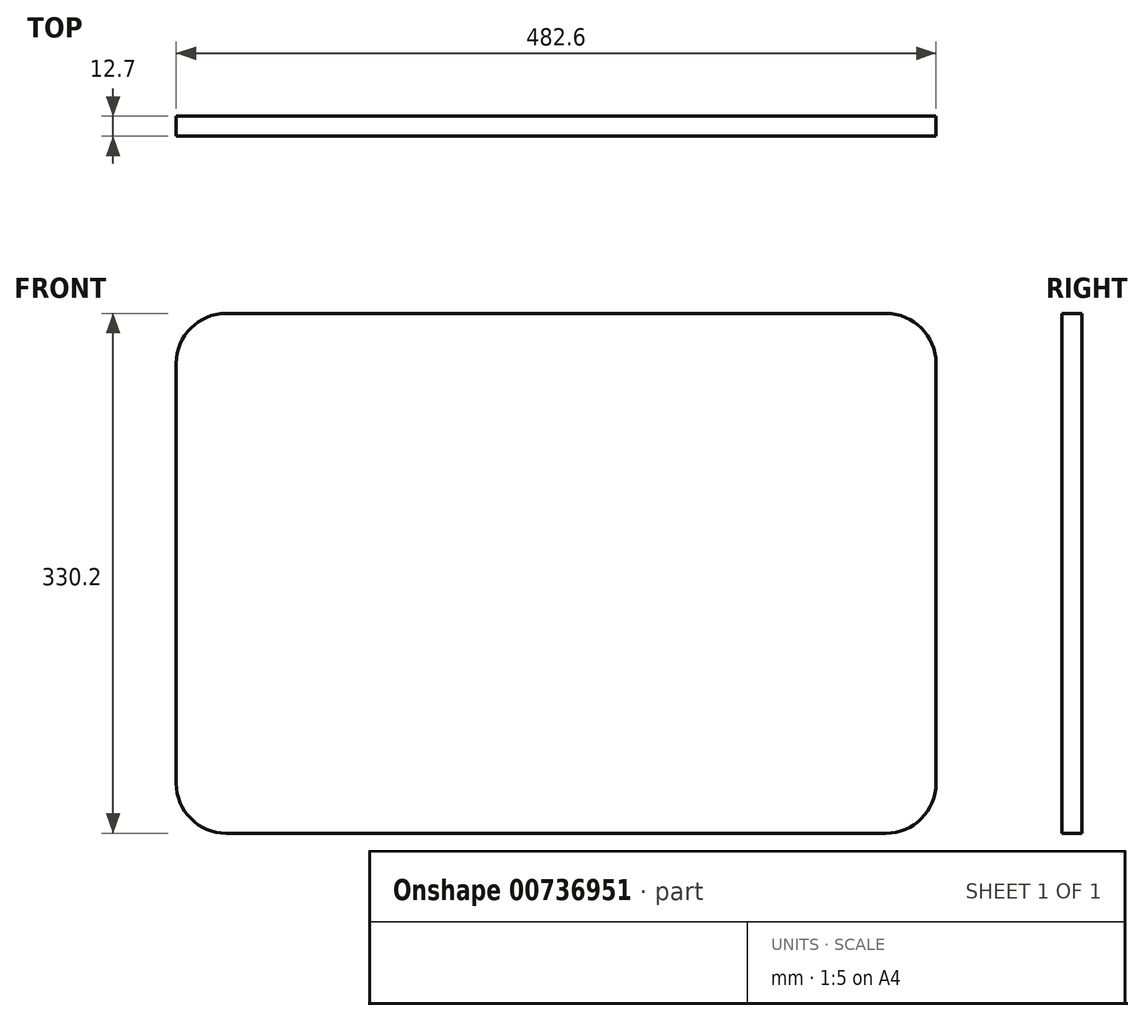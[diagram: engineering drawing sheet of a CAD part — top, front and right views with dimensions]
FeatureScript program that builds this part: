
annotation { "Feature Type Name" : "Feature", "Feature Type Description" : "" }
export const myFeature = defineFeature(function(context is Context, id is Id, definition is map)
    precondition{}
    {
        {
            var Q0;
            Q0=qCreatedBy(makeId("Front.planeOp"),FACE);
            var sketch = newSketch(context, id + "F0", { "sketchPlane" : qUnion([Q0])});
            skLineSegment(sketch, "E0.bottom", {"start": v(209.55, -165.1) * mm, "end": v(-209.55, -165.1) * mm});
            skLineSegment(sketch, "E0.top", {"start": v(209.55, 165.1) * mm, "end": v(-209.55, 165.1) * mm});
            skLineSegment(sketch, "E0.left", {"start": v(241.3, -133.35) * mm, "end": v(241.3, 133.35) * mm});
            skLineSegment(sketch, "E0.right", {"start": v(-241.3, -133.35) * mm, "end": v(-241.3, 133.35) * mm});
            skPoint(sketch, "E0.middle", {"position": v(0, 0) * mm});
            skPoint(sketch, "E1.visualSharp", {"position": v(-241.3, -165.1) * mm});
            skArc(sketch, "E1.filletArc", {"start": v(-241.3, -133.35) * mm, "mid": v(-232, -155.8) * mm, "end": v(-209.55, -165.1) * mm});
            skPoint(sketch, "E2.visualSharp", {"position": v(241.3, -165.1) * mm});
            skArc(sketch, "E2.filletArc", {"start": v(209.55, -165.1) * mm, "mid": v(232, -155.8) * mm, "end": v(241.3, -133.35) * mm});
            skPoint(sketch, "E3.visualSharp", {"position": v(-241.3, 165.1) * mm});
            skArc(sketch, "E3.filletArc", {"start": v(-209.55, 165.1) * mm, "mid": v(-232, 155.8) * mm, "end": v(-241.3, 133.35) * mm});
            skPoint(sketch, "E4.visualSharp", {"position": v(241.3, 165.1) * mm});
            skArc(sketch, "E4.filletArc", {"start": v(241.3, 133.35) * mm, "mid": v(232, 155.8) * mm, "end": v(209.55, 165.1) * mm});
            skSolve(sketch);
        }
        {
            var Q0;
            Q0=makeQuery(id+"F0.imprint","IMPRINT",FACE,{"disambiguationData":[TD([[makeQuery(id+"F0.imprint","IMPRINT",EDGE,{"derivedFrom":sQuery(id+"F0.wireOp",EDGE,"E0.bottom")}),-1.0]])]});
            extrude(context, id + "F1", {"entities" : qUnion([Q0]), "depth" : 12.7 * mm, "offsetDistance" : 25.4 * mm});
        }
    });
